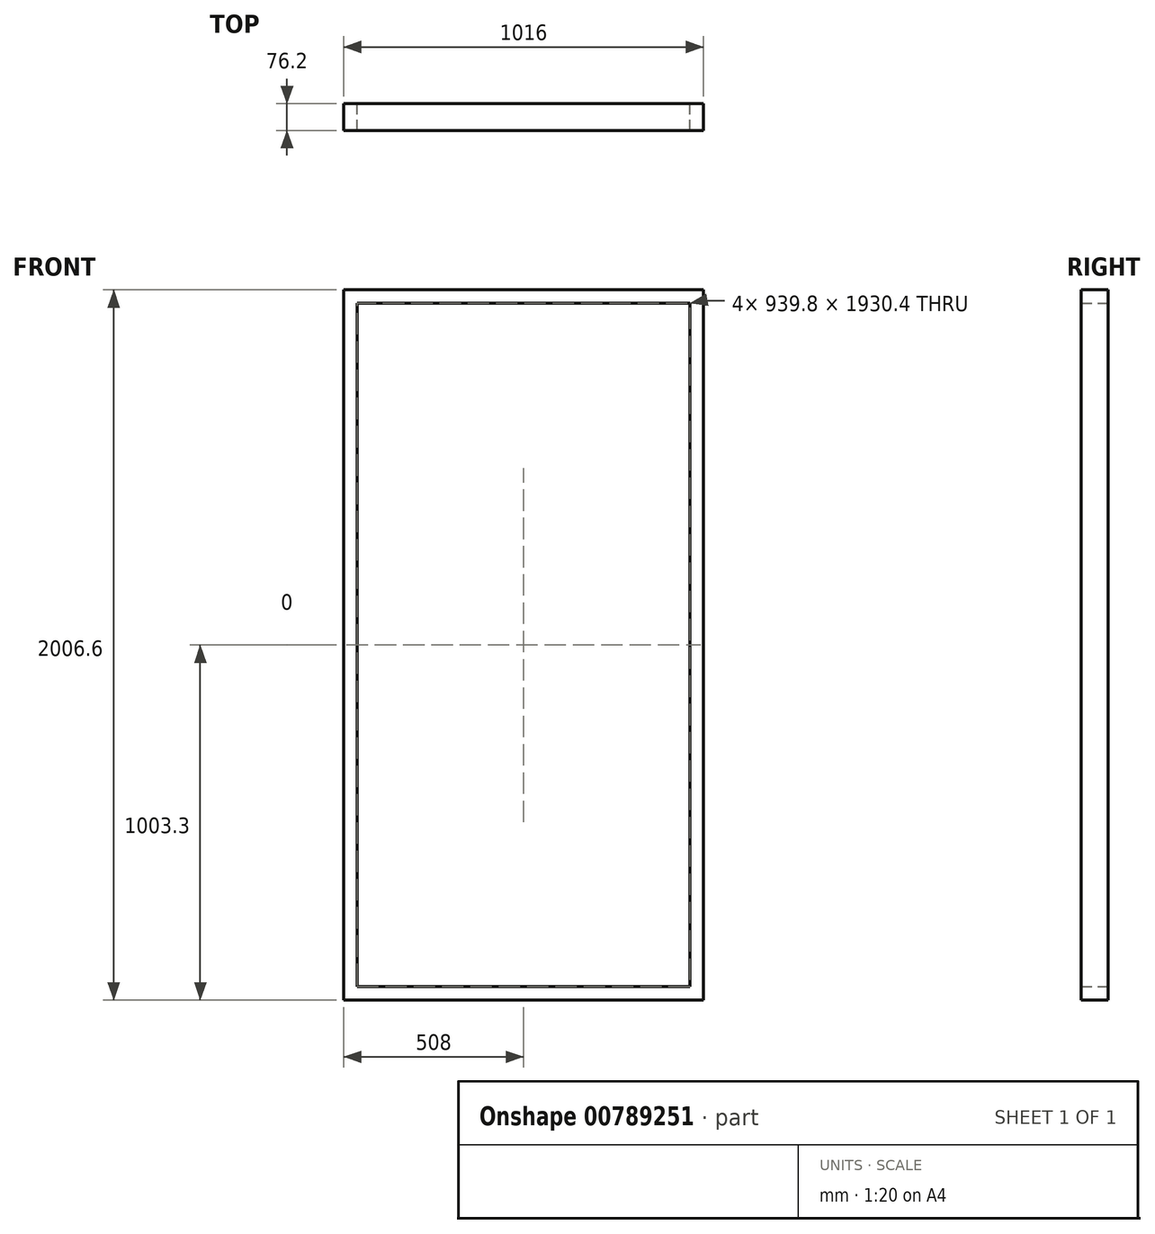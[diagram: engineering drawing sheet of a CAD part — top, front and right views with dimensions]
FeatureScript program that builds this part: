
annotation { "Feature Type Name" : "Feature", "Feature Type Description" : "" }
export const myFeature = defineFeature(function(context is Context, id is Id, definition is map)
    precondition{}
    {
        {
            var Q0;
            Q0=qCreatedBy(makeId("Front.planeOp"),FACE);
            var sketch = newSketch(context, id + "F0", { "sketchPlane" : qUnion([Q0])});
            skLineSegment(sketch, "E0.bottom", {"start": v(508, 1003.3) * mm, "end": v(-508, 1003.3) * mm});
            skLineSegment(sketch, "E0.top", {"start": v(508, -1003.3) * mm, "end": v(-508, -1003.3) * mm});
            skLineSegment(sketch, "E0.left", {"start": v(508, 1003.3) * mm, "end": v(508, -1003.3) * mm});
            skLineSegment(sketch, "E0.right", {"start": v(-508, 1003.3) * mm, "end": v(-508, -1003.3) * mm});
            skPoint(sketch, "E0.middle", {"position": v(0, 0) * mm});
            skLineSegment(sketch, "E1.bottom", {"start": v(469.9, 965.2) * mm, "end": v(-469.9, 965.2) * mm});
            skLineSegment(sketch, "E1.top", {"start": v(469.9, -965.2) * mm, "end": v(-469.9, -965.2) * mm});
            skLineSegment(sketch, "E1.left", {"start": v(469.9, 965.2) * mm, "end": v(469.9, -965.2) * mm});
            skLineSegment(sketch, "E1.right", {"start": v(-469.9, 965.2) * mm, "end": v(-469.9, -965.2) * mm});
            skSolve(sketch);
        }
        {
            var Q0;
            Q0 = qSketchRegion(id + "F0", true);
            extrude(context, id + "F1", {"entities" : qUnion([Q0]), "endBound" : BoundingType.SYMMETRIC, "depth" : 76.2 * mm, "offsetDistance" : 25.4 * mm});
        }
    });
